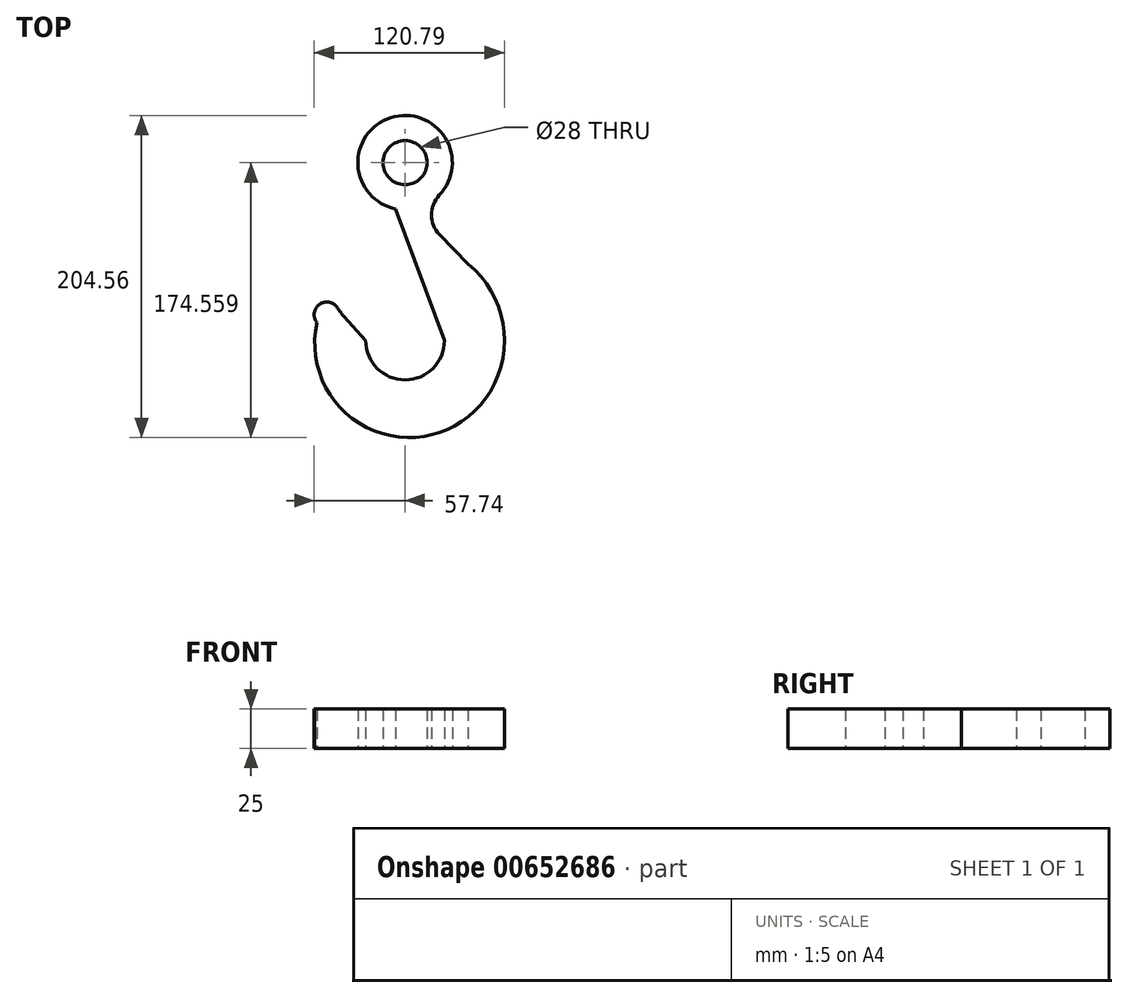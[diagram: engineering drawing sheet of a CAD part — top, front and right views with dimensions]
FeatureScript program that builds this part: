
annotation { "Feature Type Name" : "Feature", "Feature Type Description" : "" }
export const myFeature = defineFeature(function(context is Context, id is Id, definition is map)
    precondition{}
    {
        {
            var Q0;
            Q0=qCreatedBy(makeId("Top.planeOp"),FACE);
            var sketch = newSketch(context, id + "F0", { "sketchPlane" : qUnion([Q0])});
            skArc(sketch, "E0", {"start": v(21.7, 20) * mm, "mid": v(-9.01, 69.32) * mm, "end": v(-5.92, 11.3) * mm});
            skCircle(sketch, "E1", {"center": v(0, 40.7) * mm, "radius": 14 * mm});
            skLineSegment(sketch, "E2", {"start": v(-49.88, -72.3) * mm, "end": v(100.12, -72.3) * mm, "construction": true});
            skArc(sketch, "E3", {"start": v(-25, -72.3) * mm, "mid": v(0, -97.3) * mm, "end": v(25, -72.3) * mm});
            skLineSegment(sketch, "E4", {"start": v(25, -72.3) * mm, "end": v(-5.92, 11.3) * mm});
            skLineSegment(sketch, "E5", {"start": v(-5.92, 11.3) * mm, "end": v(27.08, 11.3) * mm, "construction": true});
            skLineSegment(sketch, "E6", {"start": v(21.86, -5) * mm, "end": v(40, -23.55) * mm});
            skPoint(sketch, "E7.visualSharp", {"position": v(5.92, 11.3) * mm});
            skArc(sketch, "E7.filletArc", {"start": v(21.7, 20) * mm, "mid": v(16.73, 7.47) * mm, "end": v(21.86, -5) * mm});
            skLineSegment(sketch, "E8", {"start": v(0, 92.98) * mm, "end": v(0, -212.62) * mm, "construction": true});
            skArc(sketch, "E9", {"start": v(40, -23.55) * mm, "mid": v(62.1, -61.4) * mm, "end": v(54.2, -104.51) * mm});
            skLineSegment(sketch, "E10", {"start": v(-49.88, -72.3) * mm, "end": v(-72.28, -72.3) * mm, "construction": true});
            skArc(sketch, "E11.trimOffspring", {"start": v(63.05, -72.3) * mm, "mid": v(60.8, -89) * mm, "end": v(54.2, -104.51) * mm});
            skArc(sketch, "E12.trimOffspring", {"start": v(0, -9.24) * mm, "mid": v(0.84, -9.25) * mm, "end": v(1.68, -9.26) * mm});
            skPoint(sketch, "E13.visualSharp", {"position": v(-63.05, -72.3) * mm});
            skArc(sketch, "E13.filletArc", {"start": v(-55.95, -60.83) * mm, "mid": v(-19.5, -129.62) * mm, "end": v(54.2, -104.51) * mm});
            skLineSegment(sketch, "E14", {"start": v(-49.74, -38.46) * mm, "end": v(-49.88, -88.52) * mm, "construction": true});
            skPoint(sketch, "E14.startSnap0", {"position": v(-49.74, -55.79) * mm});
            skArc(sketch, "E15", {"start": v(-43.04, -51.42) * mm, "mid": v(-54.45, -49.32) * mm, "end": v(-55.95, -60.83) * mm});
            skLineSegment(sketch, "E16", {"start": v(-38.8, -56.93) * mm, "end": v(-25, -72.3) * mm});
            skPoint(sketch, "E17.newPointB", {"position": v(-35.3, -60.83) * mm});
            skArc(sketch, "E17.filletArc", {"start": v(-43.04, -51.42) * mm, "mid": v(-41.03, -54.25) * mm, "end": v(-38.8, -56.93) * mm});
            skSolve(sketch);
        }
        {
            var Q0;
            Q0 = qSketchRegion(id + "F0", true);
            extrude(context, id + "F1", {"entities" : qUnion([Q0]), "depth" : 25 * mm, "offsetDistance" : 25 * mm});
        }
    });
